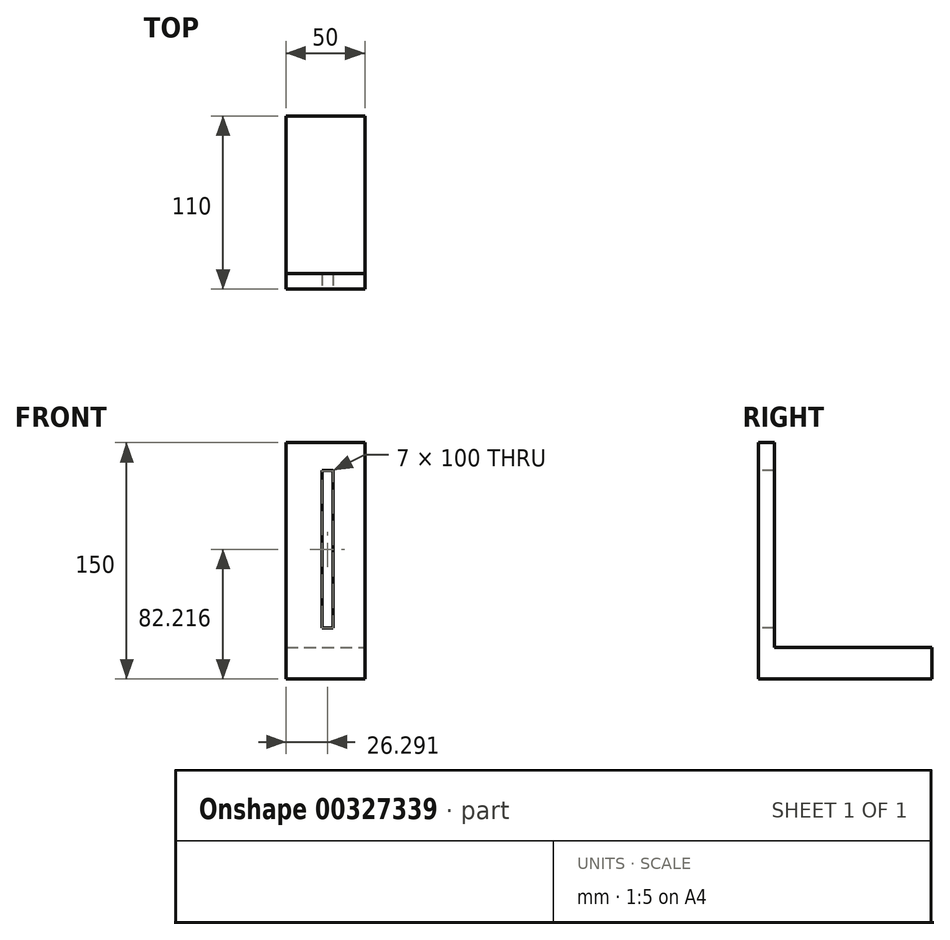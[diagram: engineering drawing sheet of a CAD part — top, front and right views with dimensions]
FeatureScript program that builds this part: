
annotation { "Feature Type Name" : "Feature", "Feature Type Description" : "" }
export const myFeature = defineFeature(function(context is Context, id is Id, definition is map)
    precondition{}
    {
        {
            var Q0;
            Q0=qCreatedBy(makeId("Top.planeOp"),FACE);
            var sketch = newSketch(context, id + "F0", { "sketchPlane" : qUnion([Q0])});
            skLineSegment(sketch, "E0.bottom", {"start": v(0, 0) * mm, "end": v(50, 0) * mm});
            skLineSegment(sketch, "E0.top", {"start": v(0, 100) * mm, "end": v(50, 100) * mm});
            skLineSegment(sketch, "E0.left", {"start": v(0, 0) * mm, "end": v(0, 100) * mm});
            skLineSegment(sketch, "E0.right", {"start": v(50, 0) * mm, "end": v(50, 100) * mm});
            skSolve(sketch);
        }
        {
            var Q0;
            Q0=makeQuery(id+"F0.imprint","IMPRINT",FACE,{"disambiguationData":[TD([[makeQuery(id+"F0.imprint","IMPRINT",EDGE,{"derivedFrom":sQuery(id+"F0.wireOp",EDGE,"E0.bottom")}),1.0]])]});
            extrude(context, id + "F1", {"entities" : qUnion([Q0]), "depth" : 20 * mm});
        }
        {
            var Q0;
            Q0=qCreatedBy(makeId("Front.planeOp"),FACE);
            var sketch = newSketch(context, id + "F2", { "sketchPlane" : qUnion([Q0])});
            skLineSegment(sketch, "E1.bottom", {"start": v(0, 0) * mm, "end": v(50, 0) * mm});
            skLineSegment(sketch, "E1.top", {"start": v(0, 150) * mm, "end": v(50, 150) * mm});
            skLineSegment(sketch, "E1.left", {"start": v(0, 0) * mm, "end": v(0, 150) * mm});
            skLineSegment(sketch, "E1.right", {"start": v(50, 0) * mm, "end": v(50, 150) * mm});
            skSolve(sketch);
        }
        {
            var Q0;
            Q0=makeQuery(id+"F2.imprint","IMPRINT",FACE,{"disambiguationData":[TD([[makeQuery(id+"F2.imprint","IMPRINT",EDGE,{"derivedFrom":sQuery(id+"F2.wireOp",EDGE,"E1.bottom")}),1.0]])]});
            extrude(context, id + "F3", {"entities" : qUnion([Q0]), "operationType" : NewBodyOperationType.ADD, "depth" : 10 * mm});
        }
        {
            var Q0;
            Q0=makeQuery(id+"F3.opExtrude","CAP_FACE",FACE,{"disambiguationData":[OSD([sQuery(id+"F2.wireOp",EDGE,"E1.bottom"),sQuery(id+"F2.wireOp",EDGE,"E1.top"),sQuery(id+"F2.wireOp",EDGE,"E1.left"),sQuery(id+"F2.wireOp",EDGE,"E1.right")])],"isStart":false});
            var sketch = newSketch(context, id + "F4", { "sketchPlane" : qUnion([Q0])});
            skSolve(sketch);
        }
        {
            var Q0;
            Q0=makeQuery(id+"F4.imprint","IMPRINT",FACE,{"disambiguationData":[TD([[makeQuery(id+"F4.imprint","IMPRINT",EDGE,{"derivedFrom":makeQuery(id+"F3.opExtrude","CAP_EDGE",EDGE,{"disambiguationData":[OSD([sQuery(id+"F2.wireOp",EDGE,"E1.bottom")])],"isStart":false})}),1.0]])]});
            var sketch = newSketch(context, id + "F5", { "sketchPlane" : qUnion([Q0])});
            skLineSegment(sketch, "E2.bottom", {"start": v(22.8, 132.22) * mm, "end": v(29.8, 132.22) * mm});
            skLineSegment(sketch, "E2.top", {"start": v(22.8, 32.22) * mm, "end": v(29.8, 32.22) * mm});
            skLineSegment(sketch, "E2.left", {"start": v(22.8, 132.22) * mm, "end": v(22.8, 32.22) * mm});
            skLineSegment(sketch, "E2.right", {"start": v(29.8, 132.22) * mm, "end": v(29.8, 32.22) * mm});
            skSolve(sketch);
        }
        {
            var Q0;
            Q0 = qSketchRegion(id + "F5", true);
            extrude(context, id + "F6", {"entities" : qUnion([Q0]), "operationType" : NewBodyOperationType.REMOVE, "oppositeDirection" : true, "depth" : 25 * mm});
        }
    });
